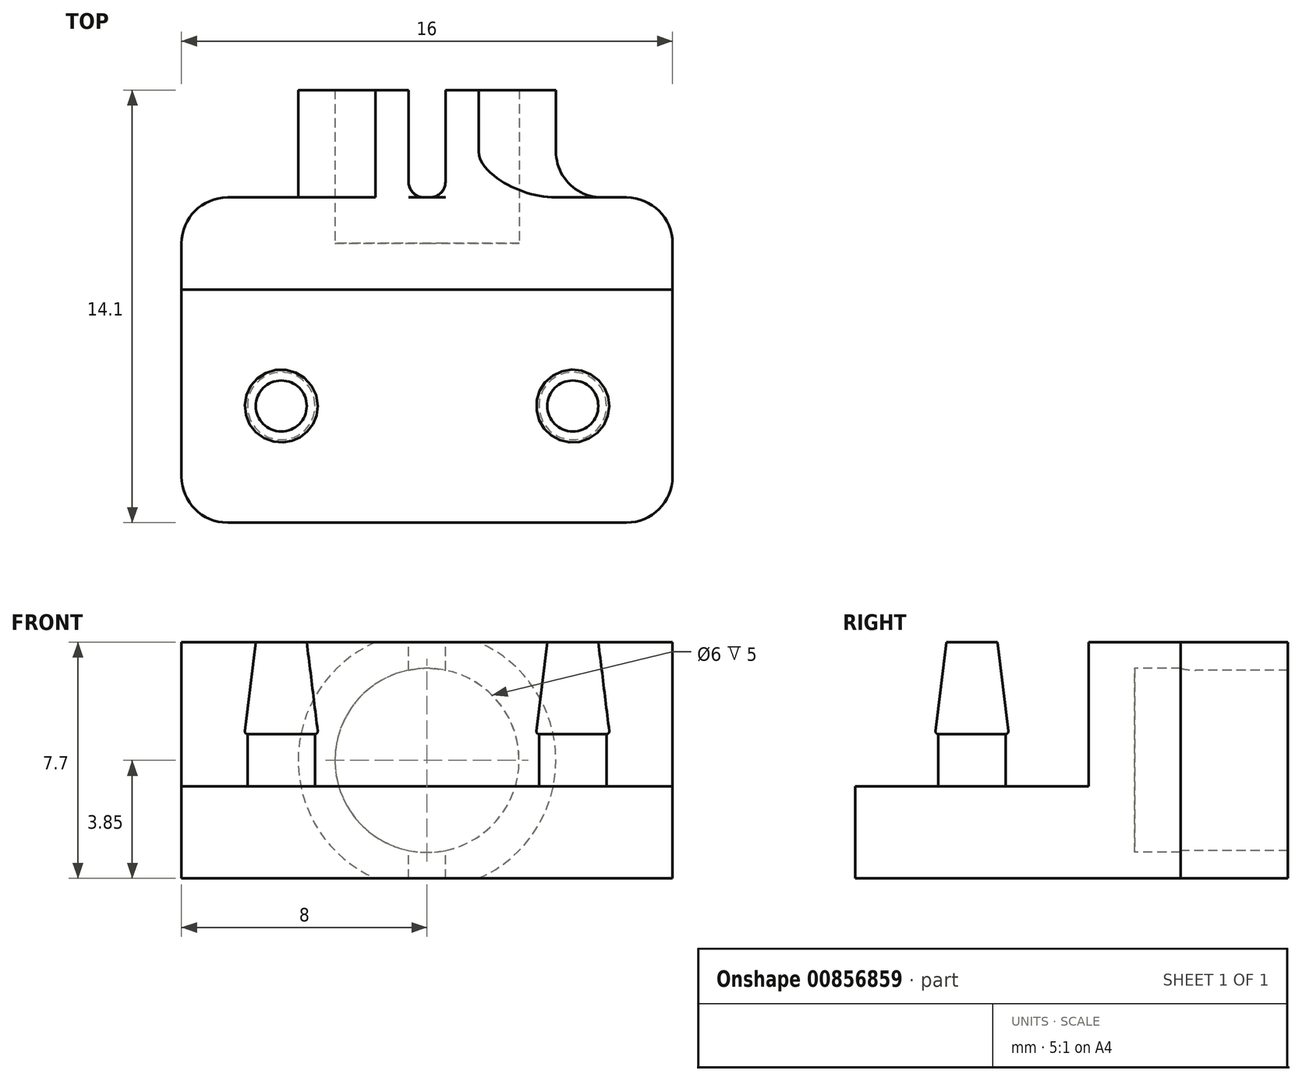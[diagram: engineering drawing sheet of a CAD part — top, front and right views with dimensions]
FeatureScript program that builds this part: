
annotation { "Feature Type Name" : "Feature", "Feature Type Description" : "" }
export const myFeature = defineFeature(function(context is Context, id is Id, definition is map)
    precondition{}
    {
        {
            var Q0;
            Q0=qCreatedBy(makeId("Top.planeOp"),FACE);
            var sketch = newSketch(context, id + "F0", { "sketchPlane" : qUnion([Q0])});
            skLineSegment(sketch, "E0.bottom", {"start": v(8, -3.8) * mm, "end": v(-8, -3.8) * mm});
            skLineSegment(sketch, "E0.top", {"start": v(8, 3.8) * mm, "end": v(-8, 3.8) * mm});
            skLineSegment(sketch, "E0.left", {"start": v(8, -3.8) * mm, "end": v(8, 3.8) * mm});
            skLineSegment(sketch, "E0.right", {"start": v(-8, -3.8) * mm, "end": v(-8, 3.8) * mm});
            skPoint(sketch, "E0.middle", {"position": v(0, 0) * mm});
            skSolve(sketch);
        }
        {
            var Q0;
            Q0=makeQuery(id+"F0.imprint","IMPRINT",FACE,{"disambiguationData":[TD([[makeQuery(id+"F0.imprint","IMPRINT",EDGE,{"derivedFrom":sQuery(id+"F0.wireOp",EDGE,"E0.bottom")}),-1.0]])]});
            extrude(context, id + "F1", {"entities" : qUnion([Q0]), "depth" : 3 * mm, "offsetDistance" : 25 * mm});
        }
        {
            var Q0;
            Q0=makeQuery(id+"F1.opExtrude","CAP_FACE",FACE,{"disambiguationData":[OSD([sQuery(id+"F0.wireOp",EDGE,"E0.bottom"),sQuery(id+"F0.wireOp",EDGE,"E0.top"),sQuery(id+"F0.wireOp",EDGE,"E0.left"),sQuery(id+"F0.wireOp",EDGE,"E0.right")])],"isStart":false});
            var sketch = newSketch(context, id + "F2", { "sketchPlane" : qUnion([Q0])});
            skCircle(sketch, "E1", {"center": v(-4.75, 0) * mm, "radius": 1.1 * mm});
            skCircle(sketch, "E2.MirrorC", {"center": v(4.75, 0) * mm, "radius": 1.1 * mm});
            skSolve(sketch);
        }
        {
            var Q0;
            Q0 = qSketchRegion(id + "F2", true);
            extrude(context, id + "F3", {"entities" : qUnion([Q0]), "operationType" : NewBodyOperationType.ADD, "depth" : 1.7 * mm, "offsetDistance" : 25 * mm, "hasDraft" : true, "draftAngle" : 0 * degree, "draftPullDirection" : true});
        }
        {
            var Q0;
            Q0=qCreatedBy(makeId("Top.planeOp"),FACE);
            var sketch = newSketch(context, id + "F4", { "sketchPlane" : qUnion([Q0])});
            skLineSegment(sketch, "E3.bottom", {"start": v(-8, 3.8) * mm, "end": v(8, 3.8) * mm});
            skLineSegment(sketch, "E3.top", {"start": v(-8, 6.8) * mm, "end": v(8, 6.8) * mm});
            skLineSegment(sketch, "E3.left", {"start": v(-8, 3.8) * mm, "end": v(-8, 6.8) * mm});
            skLineSegment(sketch, "E3.right", {"start": v(8, 3.8) * mm, "end": v(8, 6.8) * mm});
            skSolve(sketch);
        }
        {
            var Q0;
            Q0=makeQuery(id+"F3.opExtrude","CAP_FACE",FACE,{"disambiguationData":[OSD([sQuery(id+"F2.wireOp",EDGE,"E1")])],"isStart":false});
            var sketch = newSketch(context, id + "F5", { "sketchPlane" : qUnion([Q0])});
            skCircle(sketch, "E4.0", {"center": v(-4.75, 0) * mm, "radius": 1.2 * mm});
            skCircle(sketch, "E5.MirrorC", {"center": v(4.75, 0) * mm, "radius": 1.2 * mm});
            skSolve(sketch);
        }
        {
            var Q0;
            Q0 = qSketchRegion(id + "F5", true);
            extrude(context, id + "F6", {"entities" : qUnion([Q0]), "operationType" : NewBodyOperationType.ADD, "depth" : 3 * mm, "offsetDistance" : 25 * mm, "hasDraft" : true, "draftAngle" : 7 * degree, "draftPullDirection" : true});
        }
        {
            var Q0;
            Q0=makeQuery(id+"F6.opExtrude","CAP_EDGE",EDGE,{"disambiguationData":[OSD([sQuery(id+"F5.wireOp",EDGE,"E4.0")])],"isStart":true});
            var Q1;
            Q1=makeQuery(id+"F6.opExtrude","CAP_EDGE",EDGE,{"disambiguationData":[OSD([sQuery(id+"F5.wireOp",EDGE,"E5.MirrorC")])],"isStart":true});
            fillet(context, id + "F7", {"entities" : qUnion([Q0, Q1]), "radius" : 0.1 * mm, "tangentPropagation" : true, "allowEdgeOverflow" : false});
        }
        {
            var Q0;
            Q0=makeQuery(id+"F4.imprint","IMPRINT",FACE,{"disambiguationData":[TD([[makeQuery(id+"F4.imprint","IMPRINT",EDGE,{"derivedFrom":sQuery(id+"F4.wireOp",EDGE,"E3.bottom")}),1.0]])]});
            var Q1;
            Q1=makeQuery(id+"F6.opExtrude","CAP_FACE",FACE,{"disambiguationData":[OSD([sQuery(id+"F5.wireOp",EDGE,"E4.0")])],"isStart":false});
            extrude(context, id + "F8", {"entities" : qUnion([Q0]), "operationType" : NewBodyOperationType.ADD, "endBound" : BoundingType.UP_TO_SURFACE, "depth" : 6.5 * mm, "endBoundEntityFace" : qUnion([Q1]), "offsetDistance" : 25 * mm});
        }
        {
            var Q0;
            Q0=makeQuery(id+"F8.opExtrude","SWEPT_FACE",FACE,{"disambiguationData":[OSD([sQuery(id+"F4.wireOp",EDGE,"E3.top")])]});
            var sketch = newSketch(context, id + "F9", { "sketchPlane" : qUnion([Q0])});
            skCircle(sketch, "E6", {"center": v(0, 3.85) * mm, "radius": 3 * mm});
            skCircle(sketch, "E7.0", {"center": v(0, 3.85) * mm, "radius": 4.2 * mm});
            skSolve(sketch);
        }
        {
            var Q0;
            Q0=makeQuery(id+"F9.imprint","IMPRINT",FACE,{"disambiguationData":[TD([[makeQuery(id+"F9.imprint","IMPRINT",EDGE,{"derivedFrom":sQuery(id+"F9.wireOp",EDGE,"E6")}),-1.0]])]});
            extrude(context, id + "F10", {"entities" : qUnion([Q0]), "operationType" : NewBodyOperationType.ADD, "depth" : 3.5 * mm, "offsetDistance" : 25 * mm});
        }
        {
            var Q0;
            {var subQ0=sQuery(id+"F5.wireOp",EDGE,"E4.0");Q0=makeQuery(id+"F10.boolean.opBoolean","MERGE",FACE,{"derivedFrom":[makeQuery(id+"F8.opExtrude","CAP_FACE",FACE,{"disambiguationData":[OSD([subQ0])],"isStart":false}),makeQuery(id+"F10.opExtrude","SWEPT_FACE",FACE,{"disambiguationData":[OSD([sQuery(id+"F4.wireOp",EDGE,"E3.top"),subQ0])]})]});}
            var sketch = newSketch(context, id + "F11", { "sketchPlane" : qUnion([Q0])});
            skLineSegment(sketch, "E8.bottom", {"start": v(0.6, 10.3) * mm, "end": v(-0.6, 10.3) * mm});
            skLineSegment(sketch, "E8.top", {"start": v(0.6, 6.8) * mm, "end": v(-0.6, 6.8) * mm});
            skLineSegment(sketch, "E8.left", {"start": v(0.6, 10.3) * mm, "end": v(0.6, 6.8) * mm});
            skLineSegment(sketch, "E8.right", {"start": v(-0.6, 10.3) * mm, "end": v(-0.6, 6.8) * mm});
            skPoint(sketch, "E8.middle", {"position": v(0, 8.55) * mm});
            skSolve(sketch);
        }
        {
            var Q0;
            Q0=makeQuery(id+"F11.imprint","IMPRINT",FACE,{"disambiguationData":[TD([[makeQuery(id+"F11.imprint","IMPRINT",EDGE,{"derivedFrom":sQuery(id+"F11.wireOp",EDGE,"E8.bottom")}),-1.0]])]});
            var Q1;
            {var subQ0=sQuery(id+"F4.wireOp",EDGE,"E3.top");Q1=makeQuery(id+"F10.boolean.opBoolean","MERGE",FACE,{"derivedFrom":[makeQuery(id+"F8.boolean.opBoolean","MERGE",FACE,{"derivedFrom":[makeQuery(id+"F1.opExtrude","CAP_FACE",FACE,{"disambiguationData":[OSD([sQuery(id+"F0.wireOp",EDGE,"E0.bottom"),sQuery(id+"F0.wireOp",EDGE,"E0.top"),sQuery(id+"F0.wireOp",EDGE,"E0.left"),sQuery(id+"F0.wireOp",EDGE,"E0.right")])],"isStart":true}),makeQuery(id+"F8.opExtrude","CAP_FACE",FACE,{"disambiguationData":[OSD([sQuery(id+"F4.wireOp",EDGE,"E3.bottom"),subQ0,sQuery(id+"F4.wireOp",EDGE,"E3.left"),sQuery(id+"F4.wireOp",EDGE,"E3.right")])],"isStart":true})]}),makeQuery(id+"F10.opExtrude","SWEPT_FACE",FACE,{"disambiguationData":[OSD([subQ0])]})]});}
            extrude(context, id + "F12", {"entities" : qUnion([Q0]), "operationType" : NewBodyOperationType.REMOVE, "endBound" : BoundingType.UP_TO_SURFACE, "oppositeDirection" : true, "depth" : 25 * mm, "endBoundEntityFace" : qUnion([Q1]), "offsetDistance" : 25 * mm});
        }
        {
            var Q0;
            Q0=makeQuery(id+"F1.opExtrude","SWEPT_EDGE",EDGE,{"disambiguationData":[OSD([sQuery(id+"F0.wireOp",EDGE,"E0.bottom"),sQuery(id+"F0.wireOp",EDGE,"E0.right")])]});
            var Q1;
            Q1=makeQuery(id+"F1.opExtrude","SWEPT_EDGE",EDGE,{"disambiguationData":[OSD([sQuery(id+"F0.wireOp",EDGE,"E0.bottom"),sQuery(id+"F0.wireOp",EDGE,"E0.left")])]});
            var Q2;
            Q2=makeQuery(id+"F8.opExtrude","SWEPT_EDGE",EDGE,{"disambiguationData":[OSD([sQuery(id+"F4.wireOp",EDGE,"E3.top"),sQuery(id+"F4.wireOp",EDGE,"E3.left")])]});
            var Q3;
            Q3=makeQuery(id+"F8.opExtrude","SWEPT_EDGE",EDGE,{"disambiguationData":[OSD([sQuery(id+"F4.wireOp",EDGE,"E3.top"),sQuery(id+"F4.wireOp",EDGE,"E3.right")])]});
            var Q4;
            {var subQ0=sQuery(id+"F9.wireOp",EDGE,"E7.0");var subQ1=sQuery(id+"F4.wireOp",EDGE,"E3.top");Q4=makeQuery(id+"F10.opExtrude","CAP_EDGE",EDGE,{"disambiguationData":[OSD([subQ0]),TDD([makeQuery(id+"F9.imprint","IMPRINT",EDGE,{"disambiguationData":[TD([[makeQuery(id+"F9.imprint","INTERSECT",VERTEX,{"disambiguationData":[OD(1.0)],"derivedFrom":[makeQuery(id+"F8.opExtrude","CAP_EDGE",EDGE,{"disambiguationData":[OSD([subQ1])],"isStart":true}),subQ0]}),-1.0]])],"derivedFrom":subQ0})])],"isStart":true});}
            var Q5;
            {var subQ0=sQuery(id+"F9.wireOp",EDGE,"E7.0");var subQ1=sQuery(id+"F4.wireOp",EDGE,"E3.top");Q5=makeQuery(id+"F10.opExtrude","CAP_EDGE",EDGE,{"disambiguationData":[OSD([subQ0]),TDD([makeQuery(id+"F9.imprint","IMPRINT",EDGE,{"disambiguationData":[TD([[makeQuery(id+"F9.imprint","INTERSECT",VERTEX,{"disambiguationData":[OD(0.0)],"derivedFrom":[makeQuery(id+"F8.opExtrude","CAP_EDGE",EDGE,{"disambiguationData":[OSD([subQ1])],"isStart":true}),subQ0]}),1.0]])],"derivedFrom":subQ0})])],"isStart":true});}
            fillet(context, id + "F13", {"entities" : qUnion([Q0, Q1, Q2, Q3, Q4, Q5]), "radius" : 1.5 * mm, "tangentPropagation" : true, "allowEdgeOverflow" : false});
        }
        {
            var Q0;
            Q0=makeQuery(id+"F12.boolean.opBoolean","MERGE",FACE,{"derivedFrom":[makeQuery(id+"F10.boolean.opBoolean","SPLIT",FACE,{"disambiguationData":[TD([makeQuery(id+"F10.opExtrude","SWEPT_FACE",FACE,{"disambiguationData":[OSD([sQuery(id+"F9.wireOp",EDGE,"E6")])]})])],"derivedFrom":makeQuery(id+"F8.opExtrude","SWEPT_FACE",FACE,{"disambiguationData":[OSD([sQuery(id+"F4.wireOp",EDGE,"E3.top")])]})}),makeQuery(id+"F12.opExtrude","SWEPT_FACE",FACE,{"disambiguationData":[OSD([sQuery(id+"F11.wireOp",EDGE,"E8.top")])]})]});
            var sketch = newSketch(context, id + "F14", { "sketchPlane" : qUnion([Q0])});
            skCircle(sketch, "E9", {"center": v(0, 3.85) * mm, "radius": 3 * mm});
            skSolve(sketch);
        }
        {
            var Q0;
            {var subQ0=sQuery(id+"F14.wireOp",EDGE,"E9");var subQ1=sQuery(id+"F5.wireOp",EDGE,"E4.0");var subQ5=makeQuery(id+"F8.opExtrude","CAP_FACE",FACE,{"disambiguationData":[OSD([subQ1])],"isStart":false});var subQ7=sQuery(id+"F11.wireOp",EDGE,"E8.top");var subQ9=sQuery(id+"F11.wireOp",EDGE,"E8.left");var subQ11=makeQuery(id+"F12.opExtrude","SWEPT_EDGE",EDGE,{"disambiguationData":[OSD([subQ7,subQ9])]});var subQ12=makeQuery(id+"F14.imprint","INTERSECT",VERTEX,{"derivedFrom":[makeQuery(id+"F12.boolean.opBoolean","COPY",EDGE,{"disambiguationData":[TD([subQ5])],"derivedFrom":subQ11}),subQ0]});Q0=makeQuery(id+"F14.imprint","IMPRINT",FACE,{"disambiguationData":[TD([[makeQuery(id+"F14.imprint","IMPRINT",EDGE,{"disambiguationData":[TD([[subQ12,1.0]])],"derivedFrom":subQ0}),1.0]])]});}
            extrude(context, id + "F15", {"entities" : qUnion([Q0]), "operationType" : NewBodyOperationType.REMOVE, "oppositeDirection" : true, "depth" : 1.5 * mm, "offsetDistance" : 25 * mm});
        }
        {
            var Q0;
            {var subQ0=sQuery(id+"F5.wireOp",EDGE,"E4.0");var subQ2=sQuery(id+"F11.wireOp",EDGE,"E8.top");var subQ3=sQuery(id+"F11.wireOp",EDGE,"E8.right");Q0=makeQuery(id+"F12.boolean.opBoolean","COPY",EDGE,{"disambiguationData":[TD([makeQuery(id+"F8.opExtrude","CAP_FACE",FACE,{"disambiguationData":[OSD([subQ0])],"isStart":false})])],"derivedFrom":makeQuery(id+"F12.opExtrude","SWEPT_EDGE",EDGE,{"disambiguationData":[OSD([subQ2,subQ3])]})});}
            var Q1;
            {var subQ0=sQuery(id+"F5.wireOp",EDGE,"E4.0");var subQ2=sQuery(id+"F11.wireOp",EDGE,"E8.top");var subQ3=sQuery(id+"F11.wireOp",EDGE,"E8.left");Q1=makeQuery(id+"F12.boolean.opBoolean","COPY",EDGE,{"disambiguationData":[TD([makeQuery(id+"F8.opExtrude","CAP_FACE",FACE,{"disambiguationData":[OSD([subQ0])],"isStart":false})])],"derivedFrom":makeQuery(id+"F12.opExtrude","SWEPT_EDGE",EDGE,{"disambiguationData":[OSD([subQ2,subQ3])]})});}
            var Q2;
            {var subQ0=sQuery(id+"F4.wireOp",EDGE,"E3.top");var subQ1=sQuery(id+"F11.wireOp",EDGE,"E8.top");var subQ2=sQuery(id+"F11.wireOp",EDGE,"E8.left");Q2=makeQuery(id+"F12.boolean.opBoolean","COPY",EDGE,{"disambiguationData":[TD([makeQuery(id+"F10.opExtrude","SWEPT_FACE",FACE,{"disambiguationData":[OSD([subQ0])]})])],"derivedFrom":makeQuery(id+"F12.opExtrude","SWEPT_EDGE",EDGE,{"disambiguationData":[OSD([subQ1,subQ2])]})});}
            var Q3;
            {var subQ0=sQuery(id+"F4.wireOp",EDGE,"E3.top");var subQ1=sQuery(id+"F11.wireOp",EDGE,"E8.top");var subQ2=sQuery(id+"F11.wireOp",EDGE,"E8.right");Q3=makeQuery(id+"F12.boolean.opBoolean","COPY",EDGE,{"disambiguationData":[TD([makeQuery(id+"F10.opExtrude","SWEPT_FACE",FACE,{"disambiguationData":[OSD([subQ0])]})])],"derivedFrom":makeQuery(id+"F12.opExtrude","SWEPT_EDGE",EDGE,{"disambiguationData":[OSD([subQ1,subQ2])]})});}
            fillet(context, id + "F16", {"entities" : qUnion([Q0, Q1, Q2, Q3]), "radius" : 0.5 * mm, "tangentPropagation" : true, "allowEdgeOverflow" : false});
        }
    });
